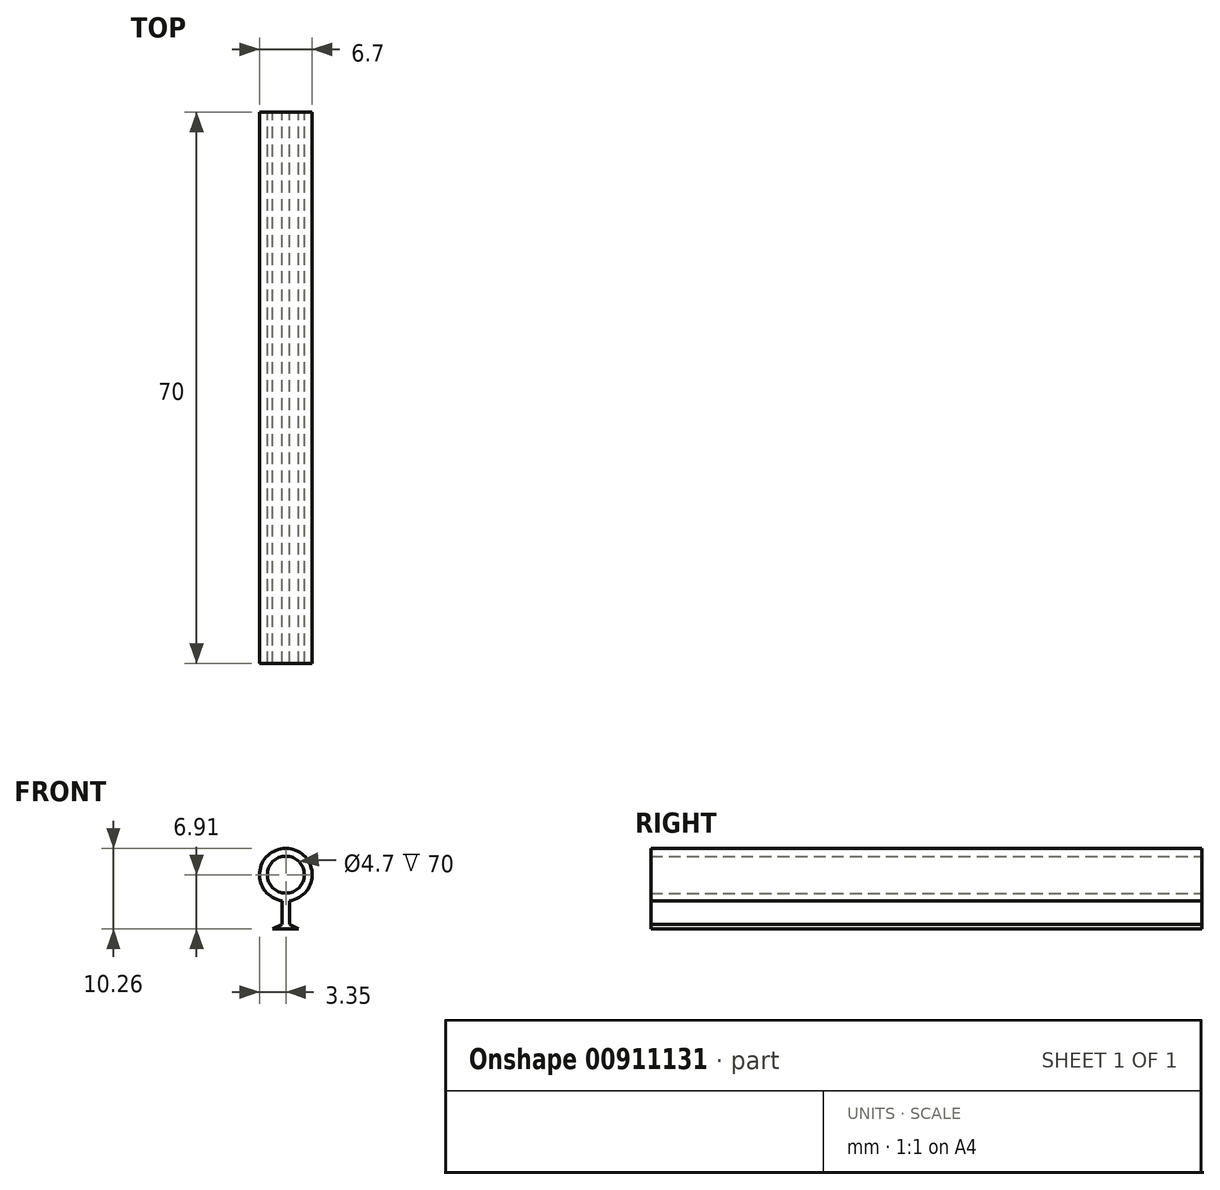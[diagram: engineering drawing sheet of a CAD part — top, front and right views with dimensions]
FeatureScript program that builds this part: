
annotation { "Feature Type Name" : "Feature", "Feature Type Description" : "" }
export const myFeature = defineFeature(function(context is Context, id is Id, definition is map)
    precondition{}
    {
        {
            var Q0;
            Q0=qCreatedBy(makeId("Front.planeOp"),FACE);
            var sketch = newSketch(context, id + "F0", { "sketchPlane" : qUnion([Q0])});
            skCircle(sketch, "E0", {"center": v(0, 0) * mm, "radius": 2.35 * mm});
            skCircle(sketch, "E1", {"center": v(0, 0) * mm, "radius": 3.35 * mm});
            skLineSegment(sketch, "E2.bottom", {"start": v(-0.5, -3.31) * mm, "end": v(0.5, -3.31) * mm});
            skLineSegment(sketch, "E2.top", {"start": v(-0.5, -6.31) * mm, "end": v(0.5, -6.31) * mm});
            skLineSegment(sketch, "E2.left", {"start": v(-0.5, -3.31) * mm, "end": v(-0.5, -6.31) * mm});
            skLineSegment(sketch, "E2.right", {"start": v(0.5, -3.31) * mm, "end": v(0.5, -6.31) * mm});
            skLineSegment(sketch, "E3", {"start": v(-0.5, -6.31) * mm, "end": v(-1.7, -6.91) * mm});
            skLineSegment(sketch, "E4", {"start": v(-1.7, -6.91) * mm, "end": v(1.63, -6.91) * mm});
            skLineSegment(sketch, "E5", {"start": v(1.63, -6.91) * mm, "end": v(0.5, -6.31) * mm});
            skSolve(sketch);
        }
        {
            var Q0;
            Q0=makeQuery(id+"F0.imprint","IMPRINT",FACE,{"disambiguationData":[TD([[makeQuery(id+"F0.imprint","IMPRINT",EDGE,{"derivedFrom":sQuery(id+"F0.wireOp",EDGE,"E2.top")}),1.0]])]});
            var Q1;
            {var subQ0=sQuery(id+"F0.wireOp",EDGE,"E2.bottom");Q1=makeQuery(id+"F0.imprint","IMPRINT",FACE,{"disambiguationData":[TD([[makeQuery(id+"F0.imprint","IMPRINT",EDGE,{"derivedFrom":subQ0}),-1.0]])]});}
            var Q2;
            Q2=makeQuery(id+"F0.imprint","IMPRINT",FACE,{"disambiguationData":[TD([[makeQuery(id+"F0.imprint","IMPRINT",EDGE,{"derivedFrom":sQuery(id+"F0.wireOp",EDGE,"E0")}),-1.0]])]});
            var Q3;
            Q3=makeQuery(id+"F0.imprint","IMPRINT",FACE,{"disambiguationData":[TD([[makeQuery(id+"F0.imprint","IMPRINT",EDGE,{"derivedFrom":sQuery(id+"F0.wireOp",EDGE,"E2.top")}),-1.0]])]});
            extrude(context, id + "F1", {"entities" : qUnion([Q0, Q1, Q2, Q3]), "depth" : 70 * mm, "offsetDistance" : 25 * mm});
        }
    });
